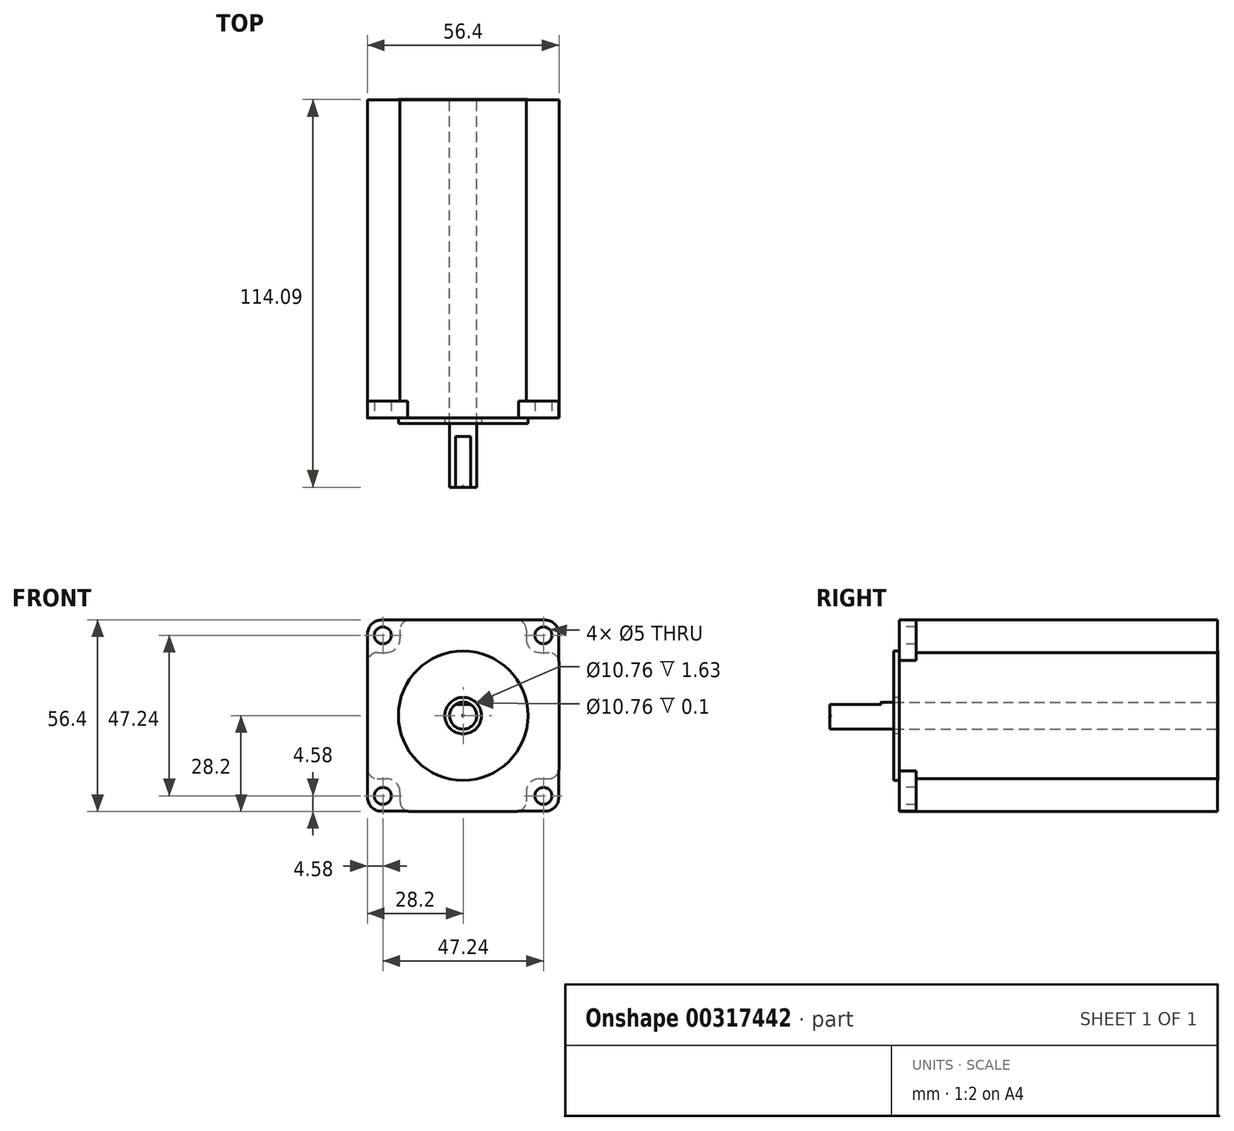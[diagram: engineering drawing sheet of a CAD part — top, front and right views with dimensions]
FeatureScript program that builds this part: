
annotation { "Feature Type Name" : "Feature", "Feature Type Description" : "" }
export const myFeature = defineFeature(function(context is Context, id is Id, definition is map)
    precondition{}
    {
        {
            var Q0;
            Q0=qCreatedBy(makeId("Front.planeOp"),FACE);
            var sketch = newSketch(context, id + "F0", { "sketchPlane" : qUnion([Q0])});
            skLineSegment(sketch, "E0.rect.bottom", {"start": v(-28.11, 28.11) * mm, "end": v(28.12, 28.11) * mm});
            skLineSegment(sketch, "E0.rect.top", {"start": v(-28.12, -28.11) * mm, "end": v(28.11, -28.11) * mm});
            skLineSegment(sketch, "E0.rect.left", {"start": v(-28.11, 28.11) * mm, "end": v(-28.12, -28.11) * mm});
            skLineSegment(sketch, "E0.rect.right", {"start": v(28.12, 28.11) * mm, "end": v(28.11, -28.11) * mm});
            skPoint(sketch, "E0.rect.middle", {"position": v(0, 0) * mm});
            skCircle(sketch, "E1", {"center": v(0, 0) * mm, "radius": 19.04 * mm});
            skCircle(sketch, "E2", {"center": v(0, 0) * mm, "radius": 3.98 * mm});
            skCircle(sketch, "E3", {"center": v(-23.62, 23.62) * mm, "radius": 2.5 * mm});
            skCircle(sketch, "E4", {"center": v(23.62, 23.62) * mm, "radius": 2.5 * mm});
            skCircle(sketch, "E5", {"center": v(23.62, -23.62) * mm, "radius": 2.5 * mm});
            skCircle(sketch, "E6", {"center": v(-23.62, -23.62) * mm, "radius": 2.5 * mm});
            skLineSegment(sketch, "E7.rect.bottom", {"start": v(-23.62, 23.62) * mm, "end": v(23.62, 23.62) * mm, "construction": true});
            skLineSegment(sketch, "E7.rect.top", {"start": v(-23.62, -23.62) * mm, "end": v(23.62, -23.62) * mm, "construction": true});
            skLineSegment(sketch, "E7.rect.left", {"start": v(-23.62, 23.62) * mm, "end": v(-23.62, -23.62) * mm, "construction": true});
            skLineSegment(sketch, "E7.rect.right", {"start": v(23.62, 23.62) * mm, "end": v(23.62, -23.62) * mm, "construction": true});
            skCircle(sketch, "E8", {"center": v(0, 0) * mm, "radius": 5.38 * mm});
            skSolve(sketch);
        }
        {
            var Q0;
            Q0=makeQuery(id+"F0.imprint","IMPRINT",FACE,{"disambiguationData":[TD([[makeQuery(id+"F0.imprint","IMPRINT",EDGE,{"derivedFrom":sQuery(id+"F0.wireOp",EDGE,"E0.rect.bottom")}),-1.0]])]});
            var Q1;
            Q1=makeQuery(id+"F0.imprint","IMPRINT",FACE,{"disambiguationData":[TD([[makeQuery(id+"F0.imprint","IMPRINT",EDGE,{"derivedFrom":sQuery(id+"F0.wireOp",EDGE,"E1")}),1.0]])]});
            var Q2;
            Q2=makeQuery(id+"F0.imprint","IMPRINT",FACE,{"disambiguationData":[TD([[makeQuery(id+"F0.imprint","IMPRINT",EDGE,{"derivedFrom":sQuery(id+"F0.wireOp",EDGE,"E2")}),1.0]])]});
            extrude(context, id + "F1", {"entities" : qUnion([Q0, Q1, Q2]), "oppositeDirection" : true, "depth" : 5 * mm});
        }
        {
            var Q0;
            Q0=makeQuery(id+"F0.imprint","IMPRINT",FACE,{"disambiguationData":[TD([[makeQuery(id+"F0.imprint","IMPRINT",EDGE,{"derivedFrom":sQuery(id+"F0.wireOp",EDGE,"E1")}),1.0]])]});
            extrude(context, id + "F2", {"entities" : qUnion([Q0]), "operationType" : NewBodyOperationType.ADD, "depth" : 1.63 * mm});
        }
        {
            var Q0;
            Q0=makeQuery(id+"F1.opExtrude","SWEPT_EDGE",EDGE,{"disambiguationData":[OSD([sQuery(id+"F0.wireOp",EDGE,"E0.rect.bottom"),sQuery(id+"F0.wireOp",EDGE,"E0.rect.left")])]});
            var Q1;
            Q1=makeQuery(id+"F1.opExtrude","SWEPT_EDGE",EDGE,{"disambiguationData":[OSD([sQuery(id+"F0.wireOp",EDGE,"E0.rect.bottom"),sQuery(id+"F0.wireOp",EDGE,"E0.rect.right")])]});
            var Q2;
            Q2=makeQuery(id+"F1.opExtrude","SWEPT_EDGE",EDGE,{"disambiguationData":[OSD([sQuery(id+"F0.wireOp",EDGE,"E0.rect.top"),sQuery(id+"F0.wireOp",EDGE,"E0.rect.right")])]});
            var Q3;
            Q3=makeQuery(id+"F1.opExtrude","SWEPT_EDGE",EDGE,{"disambiguationData":[OSD([sQuery(id+"F0.wireOp",EDGE,"E0.rect.top"),sQuery(id+"F0.wireOp",EDGE,"E0.rect.left")])]});
            fillet(context, id + "F3", {"entities" : qUnion([Q0, Q1, Q2, Q3]), "radius" : 4 * mm, "tangentPropagation" : true, "allowEdgeOverflow" : false});
        }
        {
            var Q0;
            Q0=qCreatedBy(makeId("Front.planeOp"),FACE);
            var sketch = newSketch(context, id + "F4", { "sketchPlane" : qUnion([Q0])});
            skPoint(sketch, "E9.rect.middle", {"position": v(0, 0.02) * mm});
            skPoint(sketch, "E10", {"position": v(0, 0) * mm});
            skLineSegment(sketch, "E11.rect.bottom", {"start": v(-18.57, 28.2) * mm, "end": v(18.57, 28.2) * mm});
            skLineSegment(sketch, "E11.rect.top", {"start": v(-18.57, -28.2) * mm, "end": v(18.57, -28.2) * mm});
            skLineSegment(sketch, "E11.rect.left", {"start": v(-18.57, 28.2) * mm, "end": v(-18.57, -28.2) * mm});
            skLineSegment(sketch, "E11.rect.right", {"start": v(18.57, 28.2) * mm, "end": v(18.57, -28.2) * mm});
            skLineSegment(sketch, "E12.rect.bottom", {"start": v(-28.2, 18.57) * mm, "end": v(28.2, 18.57) * mm});
            skLineSegment(sketch, "E12.rect.top", {"start": v(-28.2, -18.57) * mm, "end": v(28.2, -18.57) * mm});
            skLineSegment(sketch, "E12.rect.left", {"start": v(-28.2, 18.57) * mm, "end": v(-28.2, -18.57) * mm});
            skLineSegment(sketch, "E12.rect.right", {"start": v(28.2, 18.57) * mm, "end": v(28.2, -18.57) * mm});
            skSolve(sketch);
        }
        {
            var Q0;
            Q0=qSketchRegion(id+"F4",true);
            extrude(context, id + "F5", {"entities" : qUnion([Q0]), "operationType" : NewBodyOperationType.ADD, "oppositeDirection" : true, "depth" : 98.9 * mm});
        }
        {
            var Q0;
            Q0=makeQuery(id+"F5.opExtrude","SWEPT_EDGE",EDGE,{"disambiguationData":[OSD([sQuery(id+"F4.wireOp",EDGE,"E11.rect.right"),sQuery(id+"F4.wireOp",EDGE,"E12.rect.bottom")])]});
            var Q1;
            Q1=makeQuery(id+"F5.opExtrude","SWEPT_EDGE",EDGE,{"disambiguationData":[OSD([sQuery(id+"F4.wireOp",EDGE,"E11.rect.left"),sQuery(id+"F4.wireOp",EDGE,"E12.rect.bottom")])]});
            var Q2;
            Q2=makeQuery(id+"F5.opExtrude","SWEPT_EDGE",EDGE,{"disambiguationData":[OSD([sQuery(id+"F4.wireOp",EDGE,"E11.rect.left"),sQuery(id+"F4.wireOp",EDGE,"E12.rect.top")])]});
            var Q3;
            Q3=makeQuery(id+"F5.opExtrude","SWEPT_EDGE",EDGE,{"disambiguationData":[OSD([sQuery(id+"F4.wireOp",EDGE,"E11.rect.right"),sQuery(id+"F4.wireOp",EDGE,"E12.rect.top")])]});
            fillet(context, id + "F6", {"entities" : qUnion([Q0, Q1, Q2, Q3]), "radius" : 4 * mm, "tangentPropagation" : true, "allowEdgeOverflow" : false});
        }
        {
            var Q0;
            Q0=makeQuery(id+"F5.opExtrude","SWEPT_EDGE",EDGE,{"disambiguationData":[OSD([sQuery(id+"F4.wireOp",EDGE,"E11.rect.bottom"),sQuery(id+"F4.wireOp",EDGE,"E11.rect.right")])]});
            var Q1;
            Q1=makeQuery(id+"F5.opExtrude","SWEPT_EDGE",EDGE,{"disambiguationData":[OSD([sQuery(id+"F4.wireOp",EDGE,"E12.rect.bottom"),sQuery(id+"F4.wireOp",EDGE,"E12.rect.right")])]});
            var Q2;
            Q2=makeQuery(id+"F5.opExtrude","SWEPT_EDGE",EDGE,{"disambiguationData":[OSD([sQuery(id+"F4.wireOp",EDGE,"E12.rect.top"),sQuery(id+"F4.wireOp",EDGE,"E12.rect.right")])]});
            var Q3;
            Q3=makeQuery(id+"F5.opExtrude","SWEPT_EDGE",EDGE,{"disambiguationData":[OSD([sQuery(id+"F4.wireOp",EDGE,"E11.rect.top"),sQuery(id+"F4.wireOp",EDGE,"E11.rect.right")])]});
            var Q4;
            Q4=makeQuery(id+"F5.opExtrude","SWEPT_EDGE",EDGE,{"disambiguationData":[OSD([sQuery(id+"F4.wireOp",EDGE,"E11.rect.top"),sQuery(id+"F4.wireOp",EDGE,"E11.rect.left")])]});
            var Q5;
            Q5=makeQuery(id+"F5.opExtrude","SWEPT_EDGE",EDGE,{"disambiguationData":[OSD([sQuery(id+"F4.wireOp",EDGE,"E12.rect.top"),sQuery(id+"F4.wireOp",EDGE,"E12.rect.left")])]});
            var Q6;
            Q6=makeQuery(id+"F5.opExtrude","SWEPT_EDGE",EDGE,{"disambiguationData":[OSD([sQuery(id+"F4.wireOp",EDGE,"E12.rect.bottom"),sQuery(id+"F4.wireOp",EDGE,"E12.rect.left")])]});
            var Q7;
            Q7=makeQuery(id+"F5.opExtrude","SWEPT_EDGE",EDGE,{"disambiguationData":[OSD([sQuery(id+"F4.wireOp",EDGE,"E11.rect.bottom"),sQuery(id+"F4.wireOp",EDGE,"E11.rect.left")])]});
            fillet(context, id + "F7", {"entities" : qUnion([Q0, Q1, Q2, Q3, Q4, Q5, Q6, Q7]), "radius" : 3 * mm, "tangentPropagation" : true, "allowEdgeOverflow" : false});
        }
        {
            var Q0;
            Q0=makeQuery(id+"F0.imprint","IMPRINT",FACE,{"disambiguationData":[TD([[makeQuery(id+"F0.imprint","IMPRINT",EDGE,{"derivedFrom":sQuery(id+"F0.wireOp",EDGE,"E2")}),1.0]])]});
            extrude(context, id + "F8", {"entities" : qUnion([Q0]), "depth" : 20.4 * mm, "hasSecondDirection" : true, "secondDirectionOppositeDirection" : true, "secondDirectionDepth" : 94.9 * mm});
        }
        {
            var Q0;
            Q0=makeQuery(id+"F1.opExtrude","SWEPT_FACE",FACE,{"disambiguationData":[OSD([sQuery(id+"F0.wireOp",EDGE,"E0.rect.left")])]});
            var sketch = newSketch(context, id + "F9", { "sketchPlane" : qUnion([Q0])});
            skLineSegment(sketch, "E13", {"start": v(1.6, 3.98) * mm, "end": v(20.6, 3.98) * mm});
            skLineSegment(sketch, "E14.0", {"start": v(20.4, 3.98) * mm, "end": v(20.4, -3.98) * mm});
            skLineSegment(sketch, "E15", {"start": v(5.4, 3.98) * mm, "end": v(5.4, 3.28) * mm});
            skLineSegment(sketch, "E16", {"start": v(5.4, 3.28) * mm, "end": v(20.4, 3.28) * mm});
            skSolve(sketch);
        }
        {
            var Q0;
            Q0=qSketchRegion(id+"F9",true);
            extrude(context, id + "F10", {"entities" : qUnion([Q0]), "operationType" : NewBodyOperationType.REMOVE, "endBound" : BoundingType.THROUGH_ALL, "oppositeDirection" : true, "depth" : 31.63 * mm});
        }
        {
            var Q0;
            Q0=makeQuery(id+"F5.boolean.opBoolean","SPLIT",FACE,{"derivedFrom":makeQuery(id+"F5.opExtrude","CAP_FACE",FACE,{"disambiguationData":[OSD([sQuery(id+"F4.wireOp",EDGE,"E11.rect.bottom"),sQuery(id+"F4.wireOp",EDGE,"E11.rect.top"),sQuery(id+"F4.wireOp",EDGE,"E11.rect.left"),sQuery(id+"F4.wireOp",EDGE,"E11.rect.right"),sQuery(id+"F4.wireOp",EDGE,"E12.rect.bottom"),sQuery(id+"F4.wireOp",EDGE,"E12.rect.top"),sQuery(id+"F4.wireOp",EDGE,"E12.rect.left"),sQuery(id+"F4.wireOp",EDGE,"E12.rect.right")])],"isStart":true})});
            extrude(context, id + "F11", {"entities" : qUnion([Q0]), "operationType" : NewBodyOperationType.REMOVE, "oppositeDirection" : true, "depth" : 98.9 * mm, "hasSecondDirection" : true, "secondDirectionOppositeDirection" : true, "secondDirectionDepth" : 93.6 * mm});
        }
        {
            var Q0;
            {var subQ0=sQuery(id+"F4.wireOp",EDGE,"E12.rect.right");var subQ1=sQuery(id+"F4.wireOp",EDGE,"E12.rect.left");var subQ2=sQuery(id+"F4.wireOp",EDGE,"E12.rect.top");var subQ3=sQuery(id+"F4.wireOp",EDGE,"E12.rect.bottom");var subQ4=sQuery(id+"F4.wireOp",EDGE,"E11.rect.right");var subQ5=sQuery(id+"F4.wireOp",EDGE,"E11.rect.left");var subQ6=sQuery(id+"F4.wireOp",EDGE,"E11.rect.top");var subQ7=sQuery(id+"F4.wireOp",EDGE,"E11.rect.bottom");Q0=makeQuery(id+"F11.boolean.opBoolean","SPLIT",FACE,{"disambiguationData":[TD([makeQuery(id+"F11.opExtrude","SWEPT_FACE",FACE,{"disambiguationData":[OSD([sQuery(id+"F0.wireOp",EDGE,"E2"),subQ7,subQ6,subQ5,subQ4,subQ3,subQ2,subQ1,subQ0])]})])],"derivedFrom":makeQuery(id+"F5.opExtrude","CAP_FACE",FACE,{"disambiguationData":[OSD([subQ7,subQ6,subQ5,subQ4,subQ3,subQ2,subQ1,subQ0])],"isStart":false})});}
            extrude(context, id + "F12", {"entities" : qUnion([Q0]), "operationType" : NewBodyOperationType.REMOVE, "oppositeDirection" : true, "depth" : 5.2 * mm});
        }
        {
            var Q0;
            Q0=makeQuery(id+"F8.opExtrude","CAP_FACE",FACE,{"disambiguationData":[OSD([sQuery(id+"F0.wireOp",EDGE,"E2")])],"isStart":false});
            var sketch = newSketch(context, id + "F13", { "sketchPlane" : qUnion([Q0])});
            skCircle(sketch, "E17", {"center": v(0, 0) * mm, "radius": 0.17 * mm});
            skSolve(sketch);
        }
        {
            var Q0;
            Q0=qSketchRegion(id+"F13",true);
            extrude(context, id + "F14", {"entities" : qUnion([Q0]), "operationType" : NewBodyOperationType.REMOVE, "oppositeDirection" : true, "depth" : .5 * mm, "hasDraft" : true, "draftAngle" : 3 * degree});
        }
    });
